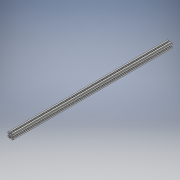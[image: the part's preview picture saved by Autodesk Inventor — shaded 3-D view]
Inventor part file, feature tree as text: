
AUTODESK INVENTOR PART (.ipt)
format: ipt  version: 2017 (Build 210142000, 142)  size: 255,488 bytes
history: native  units: in
note: dims shown in document units (in); Inventor stores cm internally (conversion verified against a paired STEP export)
features: extrude x1, sketch x1, fillet x1
ambient origin geometry x8: Origin, YZ Plane, XZ Plane, XY Plane, X Axis, Y Axis, Z Axis, Center Point
bodies: Solid1 (feature_tree)
feature tree (3):
  extrude  "Extrusion1"  [1 undecoded]
  sketch  "Sketch1"  dims[d0=22.3701in d1=0.0in]
  fillet  "Fillet6"  [1 undecoded]
note: 2 required parameter values undecoded (feature->parameter linkage not recoverable at this tier; creation-order binding heuristic only, values carry confidence <= 0.55)
